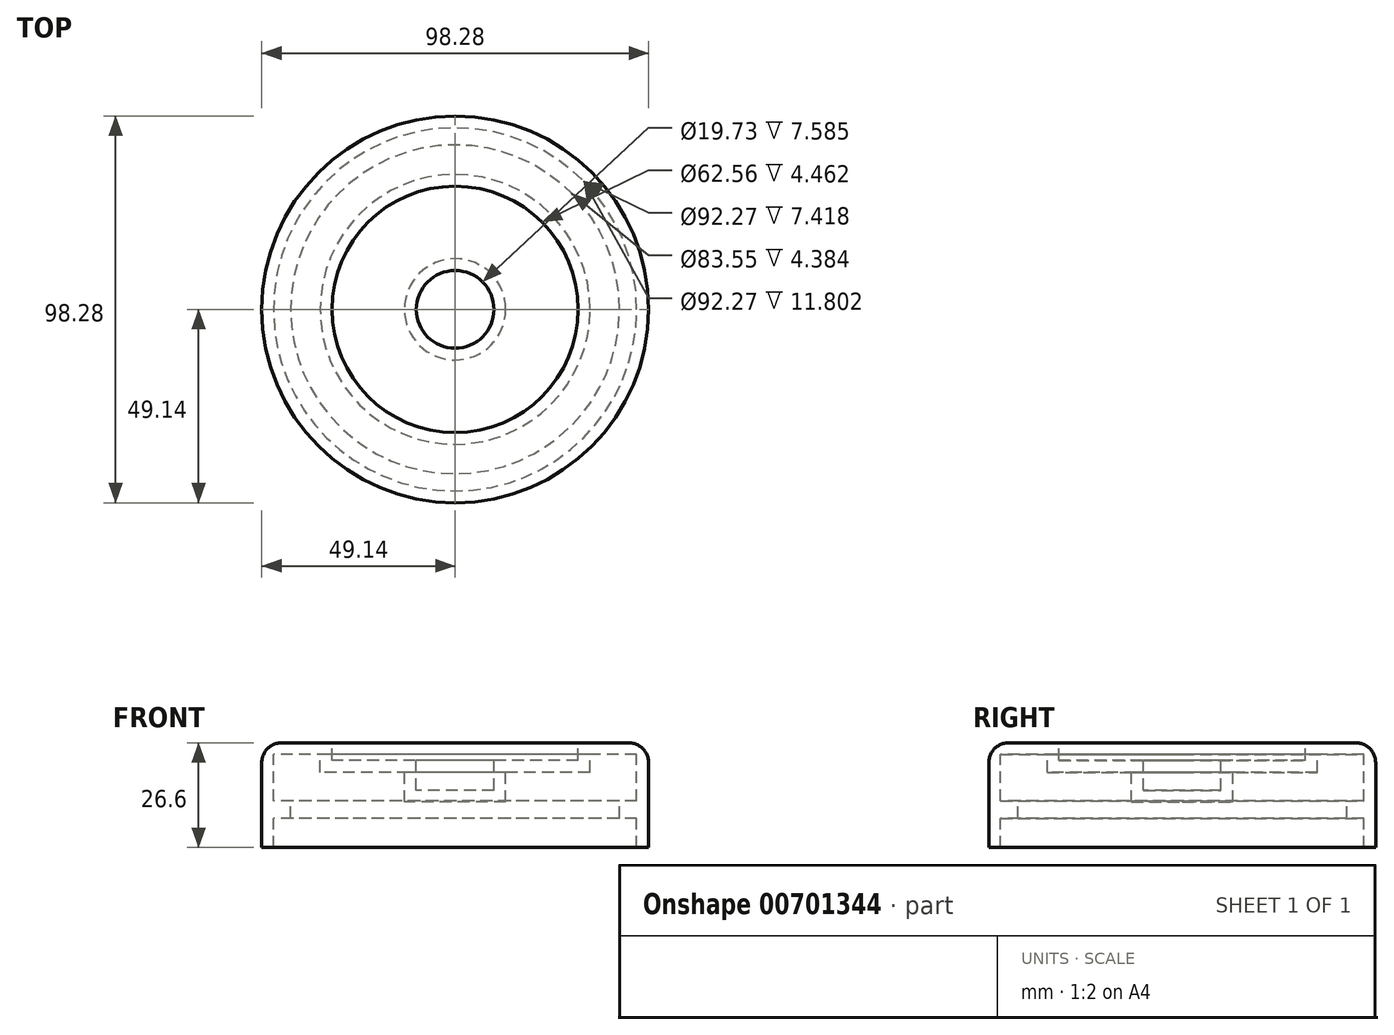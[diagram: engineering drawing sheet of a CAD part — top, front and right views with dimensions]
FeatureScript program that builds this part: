
annotation { "Feature Type Name" : "Feature", "Feature Type Description" : "" }
export const myFeature = defineFeature(function(context is Context, id is Id, definition is map)
    precondition{}
    {
        {
            var Q0;
            Q0=qCreatedBy(makeId("Front.planeOp"),FACE);
            var sketch = newSketch(context, id + "F0", { "sketchPlane" : qUnion([Q0])});
            skLineSegment(sketch, "E0", {"start": v(-49.14, 0) * mm, "end": v(-49.14, 21.6) * mm});
            skLineSegment(sketch, "E1", {"start": v(-44.14, 26.6) * mm, "end": v(-31.28, 26.6) * mm});
            skLineSegment(sketch, "E2", {"start": v(-31.28, 26.6) * mm, "end": v(-31.28, 22.14) * mm});
            skLineSegment(sketch, "E3", {"start": v(-31.28, 22.14) * mm, "end": v(-9.86, 22.14) * mm});
            skLineSegment(sketch, "E4", {"start": v(-9.86, 22.14) * mm, "end": v(-9.86, 14.56) * mm});
            skLineSegment(sketch, "E5", {"start": v(-9.86, 14.56) * mm, "end": v(0, 14.56) * mm});
            skPoint(sketch, "E6.visualSharp", {"position": v(-49.14, 26.6) * mm});
            skArc(sketch, "E6.filletArc", {"start": v(-44.14, 26.6) * mm, "mid": v(-47.67, 25.14) * mm, "end": v(-49.14, 21.6) * mm});
            skLineSegment(sketch, "E7.0", {"start": v(-12.86, 11.56) * mm, "end": v(0, 11.56) * mm});
            skLineSegment(sketch, "E7.1", {"start": v(-12.86, 19.14) * mm, "end": v(-12.86, 11.56) * mm});
            skLineSegment(sketch, "E7.3", {"start": v(-46.14, 23.6) * mm, "end": v(-34.28, 23.6) * mm});
            skLineSegment(sketch, "E7.4", {"start": v(-34.28, 23.6) * mm, "end": v(-34.28, 19.14) * mm});
            skLineSegment(sketch, "E7.5", {"start": v(-34.28, 19.14) * mm, "end": v(-12.86, 19.14) * mm});
            skLineSegment(sketch, "E8", {"start": v(-49.14, 0) * mm, "end": v(-46.14, 0) * mm});
            skLineSegment(sketch, "E9", {"start": v(0, 14.56) * mm, "end": v(0, 11.56) * mm});
            skLineSegment(sketch, "E10.bottom", {"start": v(-46.14, 11.8) * mm, "end": v(-41.77, 11.8) * mm});
            skLineSegment(sketch, "E10.top", {"start": v(-46.14, 7.42) * mm, "end": v(-41.77, 7.42) * mm});
            skLineSegment(sketch, "E10.right", {"start": v(-41.77, 11.8) * mm, "end": v(-41.77, 7.42) * mm});
            skLineSegment(sketch, "E11", {"start": v(-46.14, 11.8) * mm, "end": v(-46.14, 23.6) * mm});
            skLineSegment(sketch, "E12", {"start": v(-46.14, 7.42) * mm, "end": v(-46.14, 0) * mm});
            skSolve(sketch);
        }
        {
            var Q0;
            Q0 = qSketchRegion(id + "F0", true);
            var Q1;
            Q1=sQuery(id+"F0.wireOp",EDGE,"E9");
            revolve(context, id + "F1", {"entities" : qUnion([Q0]), "axis" : qUnion([Q1]), "revolveType" : RevolveType.FULL});
        }
    });
